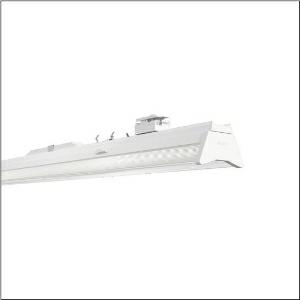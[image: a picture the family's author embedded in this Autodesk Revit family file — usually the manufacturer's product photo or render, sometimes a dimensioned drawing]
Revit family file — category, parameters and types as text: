
# Revit family: licross_r__11_performance_mo_51tm16dn445g_758e
name_source: partatom
category: Lighting Fixtures
units: mm (PartAtom-declared; Revit-internal decimal feet)

## family parameters
Cut with Voids When Loaded = No
Host = Face
Light Source = No
Part Type = Normal
Room Calculation Point = No
Round Connector Dimension = Use Diameter
Shared = No

## types (1)
- --- (1 x LED, 4520 lm, 24.3 W, 4000K)
    Apparent Load = 24 VA
    CIE Flux Codes = 66 88 96 79 100
    Color Rendering = 80
    Color Temperature = 4000K
    Default Elevation = 1800 mm
    Description = Licross® 11 Performance MO, luminaire insert, of sheet steel, galvanised, coil coated, white, length: 1.500mm, width: 120mm, height: 123mm, LED rated luminous flux: 4.520lm, light colour: 840, control gear: DALI 2, with plug, 5-pole, with phase selection, mains connection: 220..240V, AC, 50/60Hz, rated input power: 24W, halogen-free wiring, primary light control with lens, of plastic, primary optical cover: cover, of PMMA, CAT 2 (L<= 3000cd/m²), light emission: direct/indirect distribution, primary light characteristic: symmetric, protection rating (complete): IP40, insulation class (complete): insulation class I (protective earthing), certification: CE, ENEC, VDE, UKCA, protection symbol: D if used in an environment without relevant dust loads with corresponding accessories, impact resistance: IK06, permissible ambient temperature for indoor applications: -25..+45°C, corresponds to IFS (International Featured Standards) requirements for safety and quality in the food industry, reducing of maximum allowable ambient temperature of 5°C with ceiling mounting, LABS conformity tested according to VDMA 24364:2018-05, packaging unit: 1 piece
    Height = 114 mm
    Lamp = 1 x LED
    Lamp Light Flux = 4520 lm
    Lamp Power = 24.3 W
    Lamp count = 1
    Length = 1500 mm
    Luminous efficacy = 186 lm/W
    Manufacturer = Siteco
    ModVariant = No
    Model = 51TM16DN445G
    Mounting Place = Ceiling
    Mounting Type = Pendant
    Number of Poles = 1
    OnlyDefault = Yes
    Power Factor = 1
    Product Name = Licross® 11 Performance MO
    Product group = luminaire insert
    ProductGroupID = 902
    Protection Class = Protection class I
    Protection Degree = IP 40
    RLX_Detail_Level = 1
    RLX_Emergency_Light_Flux = 0 lm
    RLX_Emergency_Type = 0
    RLX_Emergency_Type_DB = No
    RlxData = <blob elided: 33801 chars, md5=b166a45d>
    Socket = socket
    Standby Power = 0 W
    System Light Flux = 4520 lm
    System Power = 24 W
    Type Comments = factory setting: luminous flux: 100 % | dim-lin: 254 | 161 mA
    Type Image = l_1256138.jpg
    URL = http://relux.com
    VarID = @adj_049456
    Voltage = 0 V
    Weight = 0.00 kg
    Width = 120 mm

## geometry (parser evidence)
native form markers: Blend x4, Sweep x13
no freeform markers — native parametric forms only
